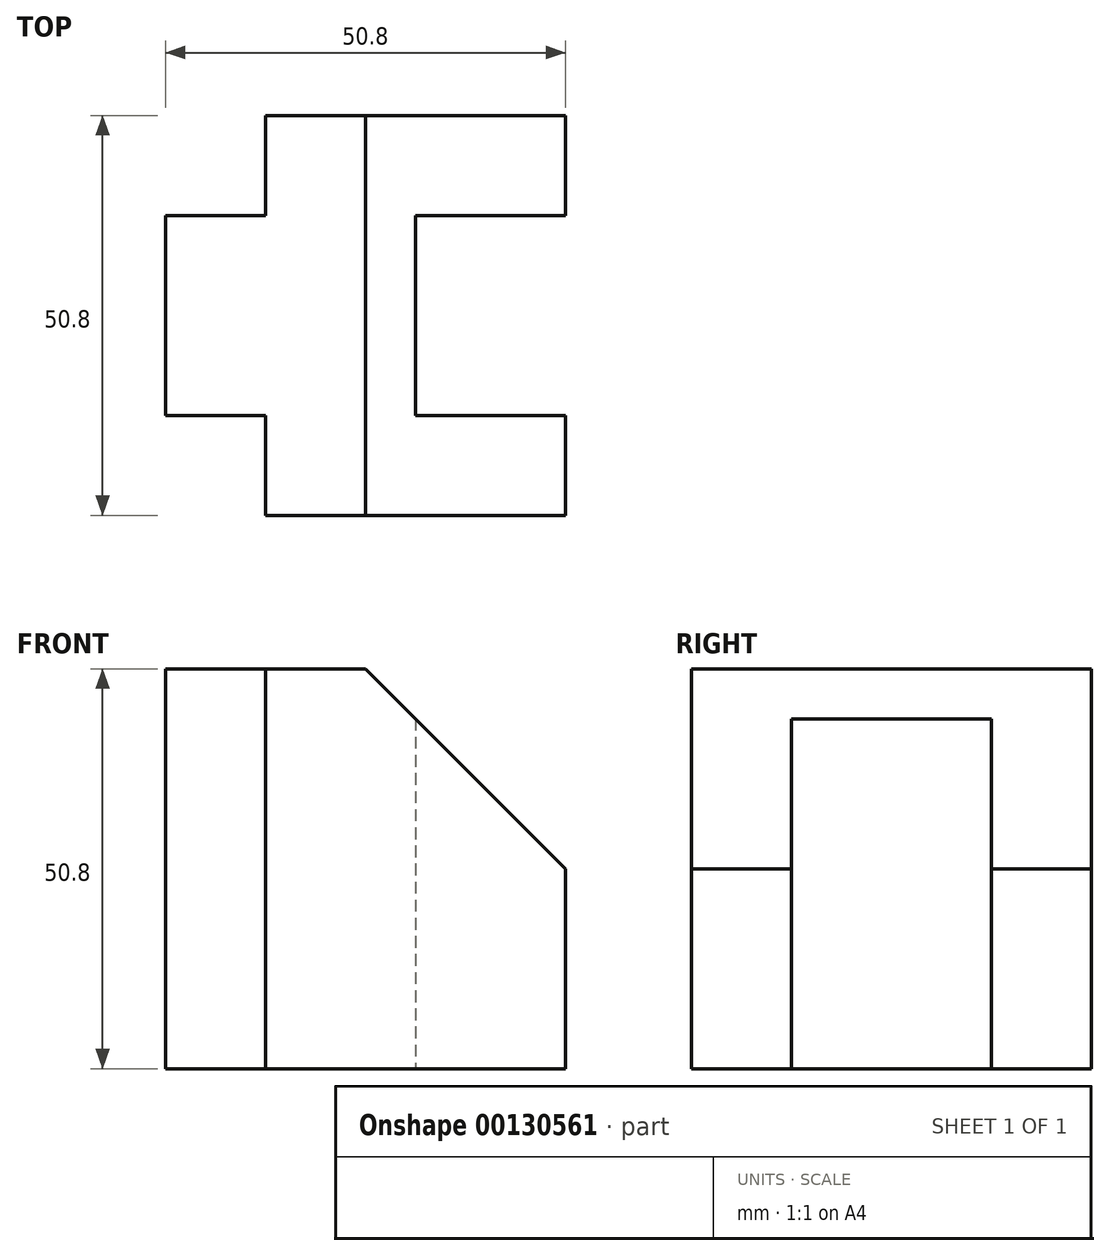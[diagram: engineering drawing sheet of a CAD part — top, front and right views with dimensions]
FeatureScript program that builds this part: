
annotation { "Feature Type Name" : "Feature", "Feature Type Description" : "" }
export const myFeature = defineFeature(function(context is Context, id is Id, definition is map)
    precondition{}
    {
        {
            var Q0;
            Q0=qCreatedBy(makeId("Top.planeOp"),FACE);
            var sketch = newSketch(context, id + "F0", { "sketchPlane" : qUnion([Q0])});
            skLineSegment(sketch, "E0", {"start": v(0, 0) * mm, "end": v(0, 12.7) * mm});
            skLineSegment(sketch, "E1", {"start": v(0, 12.7) * mm, "end": v(-12.7, 12.7) * mm});
            skLineSegment(sketch, "E2", {"start": v(-12.7, 12.7) * mm, "end": v(-12.7, 38.1) * mm});
            skLineSegment(sketch, "E3", {"start": v(-12.7, 38.1) * mm, "end": v(0, 38.1) * mm});
            skLineSegment(sketch, "E4", {"start": v(0, 38.1) * mm, "end": v(0, 50.8) * mm});
            skLineSegment(sketch, "E5", {"start": v(0, 50.8) * mm, "end": v(38.1, 50.8) * mm});
            skLineSegment(sketch, "E6", {"start": v(38.1, 50.8) * mm, "end": v(38.1, 38.1) * mm});
            skLineSegment(sketch, "E7", {"start": v(38.1, 38.1) * mm, "end": v(19.05, 38.1) * mm});
            skLineSegment(sketch, "E8", {"start": v(19.05, 38.1) * mm, "end": v(19.05, 12.7) * mm});
            skLineSegment(sketch, "E9", {"start": v(19.05, 12.7) * mm, "end": v(38.1, 12.7) * mm});
            skLineSegment(sketch, "E10", {"start": v(38.1, 12.7) * mm, "end": v(38.1, 0) * mm});
            skLineSegment(sketch, "E11", {"start": v(38.1, 0) * mm, "end": v(0, 0) * mm});
            skSolve(sketch);
        }
        {
            var Q0;
            Q0 = qSketchRegion(id + "F0", true);
            extrude(context, id + "F1", {"entities" : qUnion([Q0]), "depth" : 50.8 * mm});
        }
        {
            var Q0;
            Q0=makeQuery(id+"F1.opExtrude","SWEPT_FACE",FACE,{"disambiguationData":[OSD([sQuery(id+"F0.wireOp",EDGE,"E11")])]});
            var sketch = newSketch(context, id + "F2", { "sketchPlane" : qUnion([Q0])});
            skLineSegment(sketch, "E12", {"start": v(12.7, 50.8) * mm, "end": v(38.1, 25.4) * mm});
            skLineSegment(sketch, "E13", {"start": v(38.1, 25.4) * mm, "end": v(38.1, 50.8) * mm});
            skLineSegment(sketch, "E14", {"start": v(38.1, 50.8) * mm, "end": v(12.7, 50.8) * mm});
            skSolve(sketch);
        }
        {
            var Q0;
            Q0 = qSketchRegion(id + "F2", true);
            extrude(context, id + "F3", {"entities" : qUnion([Q0]), "operationType" : NewBodyOperationType.REMOVE, "endBound" : BoundingType.THROUGH_ALL, "oppositeDirection" : true, "depth" : 25.4 * mm});
        }
    });
